# Revit family: Haworth_Planes_HeightAdjustTable_Rectangular
name_source: partatom
category: Furniture Systems
revit_build: Autodesk Revit 2018 (Build: 20170223_1515(x64)
units: mm (PartAtom-declared; Revit-internal decimal feet)

## family parameters
Always vertical = Yes
Cut with Voids When Loaded = No
OmniClass Number = 23.40.70.14.64.21
OmniClass Title = Systems Furniture
Part Type = Normal
Room Calculation Point = No
Round Connector Dimension = Use Diameter
Shared = No
Work Plane-Based = No

## types (1)
- 70w 29d
    Actual Depth = 29"
    Actual Height = 29"
    Actual Width = 70"
    Assembly Code = E2020200
    Base Tube Finish = Haworth _ Paint _ Smoke
    Custom Size = No
    Depth = 29"
    Description = Haworth - Planes HAT Rectangular
    Edgeband = Yes
    Height = 29"
    Knife Edge = No
    Leg Depth 23 = No
    Leg Depth 29 = Yes
    Leg Height = 27 13/16"
    Leg Location = 8 3/8"
    Manufacturer = Haworth
    Max. Depth = 29"
    Max. Height = 46"
    Max. Width = 70"
    Min. Depth = 23"
    Min. Height = 27"
    Min. Width = 34"
    Min/Max Width = 34-70 in.
    Model = TARA
    Revision Number = 4
    Size = Verify Final Dim. w/ Haworth
    Standard Depths = 23, 29 in.
    Sustainability Info = http://media.haworth.com
    Table Thickness = 1 3/16"
    URL = www.haworth.com
    URL - Product = http://www.haworth.com
    Warranty = http://www.haworth.com
    Width = 70"

## geometry (parser evidence)
native form markers: Sweep x9
no freeform markers — native parametric forms only
